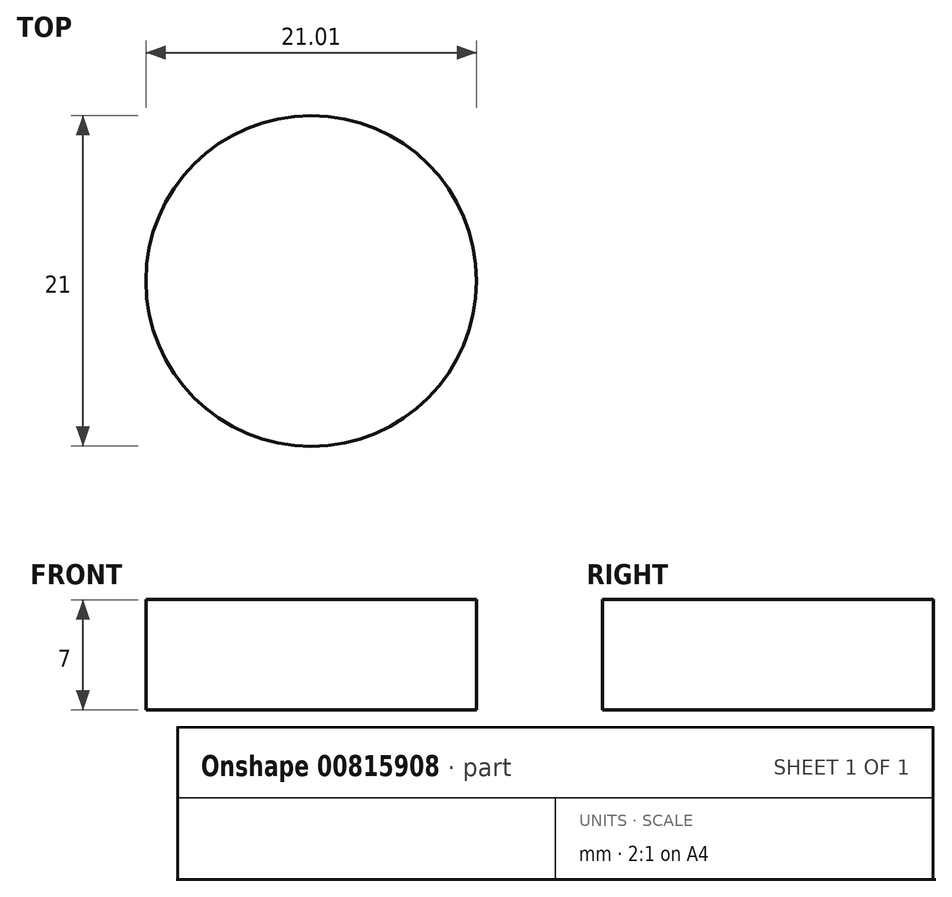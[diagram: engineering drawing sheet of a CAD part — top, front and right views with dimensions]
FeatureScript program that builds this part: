
annotation { "Feature Type Name" : "Feature", "Feature Type Description" : "" }
export const myFeature = defineFeature(function(context is Context, id is Id, definition is map)
    precondition{}
    {
        {
            var Q0;
            Q0=qCreatedBy(makeId("Front.planeOp"),FACE);
            var sketch = newSketch(context, id + "F0", { "sketchPlane" : qUnion([Q0])});
            skLineSegment(sketch, "E0.bottom", {"start": v(-8.81, -5.58) * mm, "end": v(12.19, -5.58) * mm});
            skLineSegment(sketch, "E0.top", {"start": v(-8.81, 1.42) * mm, "end": v(12.19, 1.42) * mm});
            skLineSegment(sketch, "E0.left", {"start": v(-8.81, -5.58) * mm, "end": v(-8.81, 1.42) * mm});
            skLineSegment(sketch, "E0.right", {"start": v(12.19, -5.58) * mm, "end": v(12.19, 1.42) * mm});
            skLineSegment(sketch, "E1", {"start": v(1.68, -27.18) * mm, "end": v(1.68, 10.33) * mm});
            skSolve(sketch);
        }
        {
            var Q0;
            {var subQ0=sQuery(id+"F0.wireOp",EDGE,"E0.right");Q0=makeQuery(id+"F0.imprint","IMPRINT",FACE,{"disambiguationData":[TD([[makeQuery(id+"F0.imprint","IMPRINT",EDGE,{"derivedFrom":subQ0}),1.0]])]});}
            var Q1;
            Q1=sQuery(id+"F0.wireOp",EDGE,"E1");
            revolve(context, id + "F1", {"surfaceOperationType" : NewSurfaceOperationType.NEW, "entities" : qUnion([Q0]), "axis" : qUnion([Q1]), "revolveType" : RevolveType.SYMMETRIC, "angle" : 360 * degree});
        }
    });
